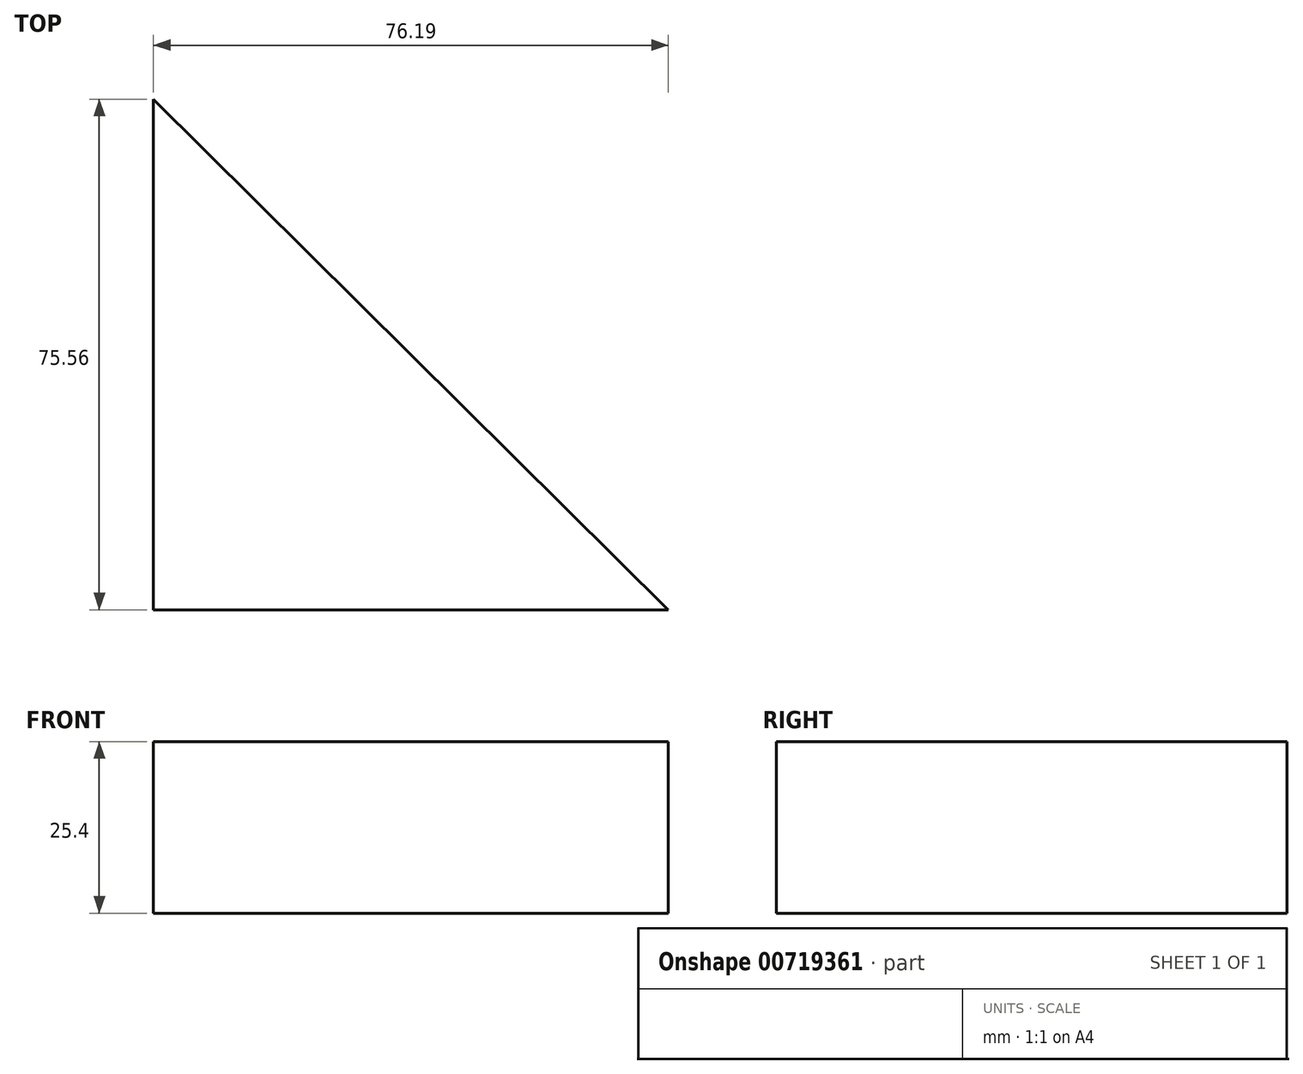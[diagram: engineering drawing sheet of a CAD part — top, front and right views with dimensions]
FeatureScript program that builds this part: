
annotation { "Feature Type Name" : "Feature", "Feature Type Description" : "" }
export const myFeature = defineFeature(function(context is Context, id is Id, definition is map)
    precondition{}
    {
        {
            var Q0;
            Q0=qCreatedBy(makeId("Top.planeOp"),FACE);
            var sketch = newSketch(context, id + "F0", { "sketchPlane" : qUnion([Q0])});
            skLineSegment(sketch, "E0", {"start": v(0, 0) * mm, "end": v(-76.2, 75.56) * mm});
            skLineSegment(sketch, "E1", {"start": v(-76.2, 75.56) * mm, "end": v(-76.2, 0) * mm});
            skLineSegment(sketch, "E2", {"start": v(-76.2, 0) * mm, "end": v(0, 0) * mm});
            skSolve(sketch);
        }
        {
            var Q0;
            Q0=makeQuery(id+"F0.imprint","IMPRINT",FACE,{"disambiguationData":[TD([[makeQuery(id+"F0.imprint","IMPRINT",EDGE,{"derivedFrom":sQuery(id+"F0.wireOp",EDGE,"E0")}),1.0]])]});
            extrude(context, id + "F1", {"entities" : qUnion([Q0]), "depth" : 25.4 * mm, "offsetDistance" : 25.4 * mm});
        }
    });
